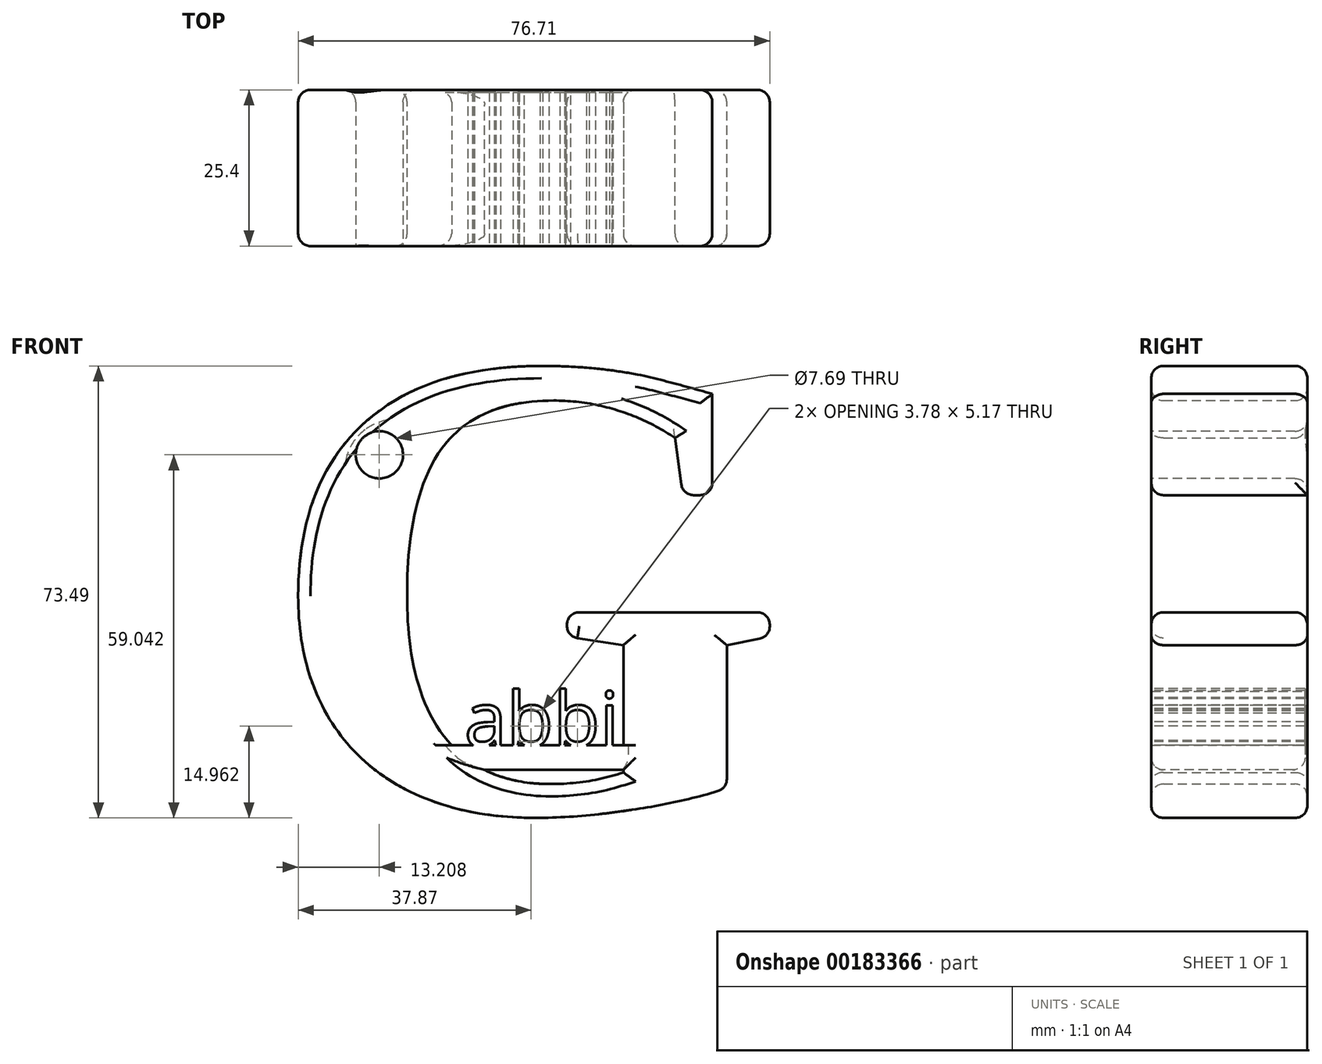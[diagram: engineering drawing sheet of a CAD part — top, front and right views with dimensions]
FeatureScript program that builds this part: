
annotation { "Feature Type Name" : "Feature", "Feature Type Description" : "" }
export const myFeature = defineFeature(function(context is Context, id is Id, definition is map)
    precondition{}
    {
        {
            var Q0;
            Q0=qCreatedBy(makeId("Front.planeOp"),FACE);
            var sketch = newSketch(context, id + "F0", { "sketchPlane" : qUnion([Q0])});
            skText(sketch, "E0", { "text": "G", "fontName": "Tinos-Bold.ttf"});
            const initialGuessF0  = {"E0": [-0.03052, -0.04578, 1, 0, 0.07873]};
            skSetInitialGuess(sketch, initialGuessF0);
            skSolve(sketch);
        }
        {
            var Q0;
            Q0 = qSketchRegion(id + "F0", true);
            extrude(context, id + "F1", {"entities" : qUnion([Q0]), "depth" : 25.4 * mm});
        }
        {
            var Q0;
            Q0=makeQuery(id+"F1.opExtrude","CAP_FACE",FACE,{"disambiguationData":[OSD([sQuery(id+"F0.wireOp",EDGE,"E0.sketch_text.stroke-0"),sQuery(id+"F0.wireOp",EDGE,"E0.sketch_text.stroke-1"),sQuery(id+"F0.wireOp",EDGE,"E0.sketch_text.stroke-2"),sQuery(id+"F0.wireOp",EDGE,"E0.sketch_text.stroke-3"),sQuery(id+"F0.wireOp",EDGE,"E0.sketch_text.stroke-4"),sQuery(id+"F0.wireOp",EDGE,"E0.sketch_text.stroke-5"),sQuery(id+"F0.wireOp",EDGE,"E0.sketch_text.stroke-6"),sQuery(id+"F0.wireOp",EDGE,"E0.sketch_text.stroke-7"),sQuery(id+"F0.wireOp",EDGE,"E0.sketch_text.stroke-8"),sQuery(id+"F0.wireOp",EDGE,"E0.sketch_text.stroke-9"),sQuery(id+"F0.wireOp",EDGE,"E0.sketch_text.stroke-10"),sQuery(id+"F0.wireOp",EDGE,"E0.sketch_text.stroke-11"),sQuery(id+"F0.wireOp",EDGE,"E0.sketch_text.stroke-12"),sQuery(id+"F0.wireOp",EDGE,"E0.sketch_text.stroke-13"),sQuery(id+"F0.wireOp",EDGE,"E0.sketch_text.stroke-14"),sQuery(id+"F0.wireOp",EDGE,"E0.sketch_text.stroke-15"),sQuery(id+"F0.wireOp",EDGE,"E0.sketch_text.stroke-16"),sQuery(id+"F0.wireOp",EDGE,"E0.sketch_text.stroke-17"),sQuery(id+"F0.wireOp",EDGE,"E0.sketch_text.stroke-18"),sQuery(id+"F0.wireOp",EDGE,"E0.sketch_text.stroke-19"),sQuery(id+"F0.wireOp",EDGE,"E0.sketch_text.stroke-20"),sQuery(id+"F0.wireOp",EDGE,"E0.sketch_text.stroke-21"),sQuery(id+"F0.wireOp",EDGE,"E0.sketch_text.stroke-22"),sQuery(id+"F0.wireOp",EDGE,"E0.sketch_text.stroke-23"),sQuery(id+"F0.wireOp",EDGE,"E0.sketch_text.stroke-24"),sQuery(id+"F0.wireOp",EDGE,"E0.sketch_text.stroke-25"),sQuery(id+"F0.wireOp",EDGE,"E0.sketch_text.stroke-26")])],"isStart":false});
            var sketch = newSketch(context, id + "F2", { "sketchPlane" : qUnion([Q0])});
            skCircle(sketch, "E1", {"center": v(-11.96, 12.18) * mm, "radius": 3.84 * mm});
            skSolve(sketch);
        }
        {
            var Q0;
            Q0=makeQuery(id+"F2.imprint","IMPRINT",FACE,{"disambiguationData":[TD([[makeQuery(id+"F2.imprint","IMPRINT",EDGE,{"derivedFrom":sQuery(id+"F2.wireOp",EDGE,"E1")}),1.0]])]});
            extrude(context, id + "F3", {"entities" : qUnion([Q0]), "operationType" : NewBodyOperationType.REMOVE, "oppositeDirection" : true, "depth" : 27.94 * mm});
        }
        {
            var Q0;
            Q0=makeQuery(id+"F1.opExtrude","CAP_EDGE",EDGE,{"disambiguationData":[OSD([sQuery(id+"F0.wireOp",EDGE,"E0.sketch_text.stroke-9")])],"isStart":false});
            var Q1;
            Q1=makeQuery(id+"F1.opExtrude","CAP_EDGE",EDGE,{"disambiguationData":[OSD([sQuery(id+"F0.wireOp",EDGE,"E0.sketch_text.stroke-15")])],"isStart":false});
            var Q2;
            Q2=makeQuery(id+"F1.opExtrude","CAP_EDGE",EDGE,{"disambiguationData":[OSD([sQuery(id+"F0.wireOp",EDGE,"E0.sketch_text.stroke-20")])],"isStart":false});
            var Q3;
            Q3=makeQuery(id+"F1.opExtrude","CAP_EDGE",EDGE,{"disambiguationData":[OSD([sQuery(id+"F0.wireOp",EDGE,"E0.sketch_text.stroke-21")])],"isStart":false});
            var Q4;
            Q4=makeQuery(id+"F1.opExtrude","CAP_EDGE",EDGE,{"disambiguationData":[OSD([sQuery(id+"F0.wireOp",EDGE,"E0.sketch_text.stroke-22")])],"isStart":false});
            var Q5;
            Q5=makeQuery(id+"F1.opExtrude","CAP_EDGE",EDGE,{"disambiguationData":[OSD([sQuery(id+"F0.wireOp",EDGE,"E0.sketch_text.stroke-24")])],"isStart":false});
            var Q6;
            Q6=makeQuery(id+"F1.opExtrude","CAP_EDGE",EDGE,{"disambiguationData":[OSD([sQuery(id+"F0.wireOp",EDGE,"E0.sketch_text.stroke-26")])],"isStart":false});
            var Q7;
            Q7=makeQuery(id+"F1.opExtrude","CAP_EDGE",EDGE,{"disambiguationData":[OSD([sQuery(id+"F0.wireOp",EDGE,"E0.sketch_text.stroke-23")])],"isStart":false});
            var Q8;
            Q8=makeQuery(id+"F1.opExtrude","CAP_EDGE",EDGE,{"disambiguationData":[OSD([sQuery(id+"F0.wireOp",EDGE,"E0.sketch_text.stroke-12")])],"isStart":false});
            var Q9;
            Q9=makeQuery(id+"F1.opExtrude","CAP_EDGE",EDGE,{"disambiguationData":[OSD([sQuery(id+"F0.wireOp",EDGE,"E0.sketch_text.stroke-10")])],"isStart":false});
            var Q10;
            Q10=makeQuery(id+"F1.opExtrude","CAP_EDGE",EDGE,{"disambiguationData":[OSD([sQuery(id+"F0.wireOp",EDGE,"E0.sketch_text.stroke-11")])],"isStart":false});
            var Q11;
            Q11=makeQuery(id+"F1.opExtrude","SWEPT_EDGE",EDGE,{"disambiguationData":[OSD([sQuery(id+"F0.wireOp",EDGE,"E0.sketch_text.stroke-11"),sQuery(id+"F0.wireOp",EDGE,"E0.sketch_text.stroke-12")])]});
            var Q12;
            Q12=makeQuery(id+"F1.opExtrude","SWEPT_EDGE",EDGE,{"disambiguationData":[OSD([sQuery(id+"F0.wireOp",EDGE,"E0.sketch_text.stroke-10"),sQuery(id+"F0.wireOp",EDGE,"E0.sketch_text.stroke-11")])]});
            var Q13;
            Q13=makeQuery(id+"F1.opExtrude","CAP_EDGE",EDGE,{"disambiguationData":[OSD([sQuery(id+"F0.wireOp",EDGE,"E0.sketch_text.stroke-25")])],"isStart":false});
            var Q14;
            Q14=makeQuery(id+"F3.boolean.opBoolean","COPY",EDGE,{"derivedFrom":makeQuery(id+"F3.opExtrude","CAP_EDGE",EDGE,{"disambiguationData":[OSD([sQuery(id+"F2.wireOp",EDGE,"E1")])],"isStart":true})});
            var Q15;
            Q15=makeQuery(id+"F3.boolean.opBoolean","INTERSECT",EDGE,{"derivedFrom":[makeQuery(id+"F1.opExtrude","CAP_FACE",FACE,{"disambiguationData":[OSD([sQuery(id+"F0.wireOp",EDGE,"E0.sketch_text.stroke-0"),sQuery(id+"F0.wireOp",EDGE,"E0.sketch_text.stroke-1"),sQuery(id+"F0.wireOp",EDGE,"E0.sketch_text.stroke-2"),sQuery(id+"F0.wireOp",EDGE,"E0.sketch_text.stroke-3"),sQuery(id+"F0.wireOp",EDGE,"E0.sketch_text.stroke-4"),sQuery(id+"F0.wireOp",EDGE,"E0.sketch_text.stroke-5"),sQuery(id+"F0.wireOp",EDGE,"E0.sketch_text.stroke-6"),sQuery(id+"F0.wireOp",EDGE,"E0.sketch_text.stroke-7"),sQuery(id+"F0.wireOp",EDGE,"E0.sketch_text.stroke-8"),sQuery(id+"F0.wireOp",EDGE,"E0.sketch_text.stroke-9"),sQuery(id+"F0.wireOp",EDGE,"E0.sketch_text.stroke-10"),sQuery(id+"F0.wireOp",EDGE,"E0.sketch_text.stroke-11"),sQuery(id+"F0.wireOp",EDGE,"E0.sketch_text.stroke-12"),sQuery(id+"F0.wireOp",EDGE,"E0.sketch_text.stroke-13"),sQuery(id+"F0.wireOp",EDGE,"E0.sketch_text.stroke-14"),sQuery(id+"F0.wireOp",EDGE,"E0.sketch_text.stroke-15"),sQuery(id+"F0.wireOp",EDGE,"E0.sketch_text.stroke-16"),sQuery(id+"F0.wireOp",EDGE,"E0.sketch_text.stroke-17"),sQuery(id+"F0.wireOp",EDGE,"E0.sketch_text.stroke-18"),sQuery(id+"F0.wireOp",EDGE,"E0.sketch_text.stroke-19"),sQuery(id+"F0.wireOp",EDGE,"E0.sketch_text.stroke-20"),sQuery(id+"F0.wireOp",EDGE,"E0.sketch_text.stroke-21"),sQuery(id+"F0.wireOp",EDGE,"E0.sketch_text.stroke-22"),sQuery(id+"F0.wireOp",EDGE,"E0.sketch_text.stroke-23"),sQuery(id+"F0.wireOp",EDGE,"E0.sketch_text.stroke-24"),sQuery(id+"F0.wireOp",EDGE,"E0.sketch_text.stroke-25"),sQuery(id+"F0.wireOp",EDGE,"E0.sketch_text.stroke-26")])],"isStart":true}),makeQuery(id+"F3.opExtrude","SWEPT_FACE",FACE,{"disambiguationData":[OSD([sQuery(id+"F2.wireOp",EDGE,"E1")])]})]});
            var Q16;
            Q16=makeQuery(id+"F1.opExtrude","CAP_EDGE",EDGE,{"disambiguationData":[OSD([sQuery(id+"F0.wireOp",EDGE,"E0.sketch_text.stroke-26")])],"isStart":true});
            var Q17;
            Q17=makeQuery(id+"F1.opExtrude","SWEPT_EDGE",EDGE,{"disambiguationData":[OSD([sQuery(id+"F0.wireOp",EDGE,"E0.sketch_text.stroke-0"),sQuery(id+"F0.wireOp",EDGE,"E0.sketch_text.stroke-26")])]});
            var Q18;
            Q18=makeQuery(id+"F1.opExtrude","CAP_EDGE",EDGE,{"disambiguationData":[OSD([sQuery(id+"F0.wireOp",EDGE,"E0.sketch_text.stroke-23")])],"isStart":true});
            var Q19;
            Q19=makeQuery(id+"F1.opExtrude","CAP_EDGE",EDGE,{"disambiguationData":[OSD([sQuery(id+"F0.wireOp",EDGE,"E0.sketch_text.stroke-22")])],"isStart":true});
            var Q20;
            Q20=makeQuery(id+"F1.opExtrude","SWEPT_EDGE",EDGE,{"disambiguationData":[OSD([sQuery(id+"F0.wireOp",EDGE,"E0.sketch_text.stroke-22"),sQuery(id+"F0.wireOp",EDGE,"E0.sketch_text.stroke-23")])]});
            var Q21;
            Q21=makeQuery(id+"F1.opExtrude","SWEPT_EDGE",EDGE,{"disambiguationData":[OSD([sQuery(id+"F0.wireOp",EDGE,"E0.sketch_text.stroke-24"),sQuery(id+"F0.wireOp",EDGE,"E0.sketch_text.stroke-25")])]});
            var Q22;
            Q22=makeQuery(id+"F1.opExtrude","SWEPT_EDGE",EDGE,{"disambiguationData":[OSD([sQuery(id+"F0.wireOp",EDGE,"E0.sketch_text.stroke-23"),sQuery(id+"F0.wireOp",EDGE,"E0.sketch_text.stroke-24")])]});
            var Q23;
            Q23=makeQuery(id+"F1.opExtrude","CAP_EDGE",EDGE,{"disambiguationData":[OSD([sQuery(id+"F0.wireOp",EDGE,"E0.sketch_text.stroke-9")])],"isStart":true});
            var Q24;
            Q24=makeQuery(id+"F1.opExtrude","CAP_EDGE",EDGE,{"disambiguationData":[OSD([sQuery(id+"F0.wireOp",EDGE,"E0.sketch_text.stroke-10")])],"isStart":true});
            fillet(context, id + "F4", {"entities" : qUnion([Q0, Q1, Q2, Q3, Q4, Q5, Q6, Q7, Q8, Q9, Q10, Q11, Q12, Q13, Q14, Q15, Q16, Q17, Q18, Q19, Q20, Q21, Q22, Q23, Q24]), "radius" : 2 * mm, "tangentPropagation" : true, "allowEdgeOverflow" : false});
        }
        {
            var Q0;
            Q0=makeQuery(id+"F1.opExtrude","CAP_EDGE",EDGE,{"disambiguationData":[OSD([sQuery(id+"F0.wireOp",EDGE,"E0.sketch_text.stroke-15")])],"isStart":true});
            var Q1;
            Q1=makeQuery(id+"F1.opExtrude","CAP_EDGE",EDGE,{"disambiguationData":[OSD([sQuery(id+"F0.wireOp",EDGE,"E0.sketch_text.stroke-21")])],"isStart":true});
            var Q2;
            Q2=makeQuery(id+"F1.opExtrude","CAP_EDGE",EDGE,{"disambiguationData":[OSD([sQuery(id+"F0.wireOp",EDGE,"E0.sketch_text.stroke-20")])],"isStart":true});
            fillet(context, id + "F5", {"entities" : qUnion([Q0, Q1, Q2]), "radius" : 2 * mm, "tangentPropagation" : true, "allowEdgeOverflow" : false});
        }
        {
            var Q0;
            Q0=makeQuery(id+"F1.opExtrude","CAP_FACE",FACE,{"disambiguationData":[OSD([sQuery(id+"F0.wireOp",EDGE,"E0.sketch_text.stroke-0"),sQuery(id+"F0.wireOp",EDGE,"E0.sketch_text.stroke-1"),sQuery(id+"F0.wireOp",EDGE,"E0.sketch_text.stroke-2"),sQuery(id+"F0.wireOp",EDGE,"E0.sketch_text.stroke-3"),sQuery(id+"F0.wireOp",EDGE,"E0.sketch_text.stroke-4"),sQuery(id+"F0.wireOp",EDGE,"E0.sketch_text.stroke-5"),sQuery(id+"F0.wireOp",EDGE,"E0.sketch_text.stroke-6"),sQuery(id+"F0.wireOp",EDGE,"E0.sketch_text.stroke-7"),sQuery(id+"F0.wireOp",EDGE,"E0.sketch_text.stroke-8"),sQuery(id+"F0.wireOp",EDGE,"E0.sketch_text.stroke-9"),sQuery(id+"F0.wireOp",EDGE,"E0.sketch_text.stroke-10"),sQuery(id+"F0.wireOp",EDGE,"E0.sketch_text.stroke-11"),sQuery(id+"F0.wireOp",EDGE,"E0.sketch_text.stroke-12"),sQuery(id+"F0.wireOp",EDGE,"E0.sketch_text.stroke-13"),sQuery(id+"F0.wireOp",EDGE,"E0.sketch_text.stroke-14"),sQuery(id+"F0.wireOp",EDGE,"E0.sketch_text.stroke-15"),sQuery(id+"F0.wireOp",EDGE,"E0.sketch_text.stroke-16"),sQuery(id+"F0.wireOp",EDGE,"E0.sketch_text.stroke-17"),sQuery(id+"F0.wireOp",EDGE,"E0.sketch_text.stroke-18"),sQuery(id+"F0.wireOp",EDGE,"E0.sketch_text.stroke-19"),sQuery(id+"F0.wireOp",EDGE,"E0.sketch_text.stroke-20"),sQuery(id+"F0.wireOp",EDGE,"E0.sketch_text.stroke-21"),sQuery(id+"F0.wireOp",EDGE,"E0.sketch_text.stroke-22"),sQuery(id+"F0.wireOp",EDGE,"E0.sketch_text.stroke-23"),sQuery(id+"F0.wireOp",EDGE,"E0.sketch_text.stroke-24"),sQuery(id+"F0.wireOp",EDGE,"E0.sketch_text.stroke-25"),sQuery(id+"F0.wireOp",EDGE,"E0.sketch_text.stroke-26")])],"isStart":false});
            var sketch = newSketch(context, id + "F6", { "sketchPlane" : qUnion([Q0])});
            skText(sketch, "E2", { "text": "abbi\n", "fontName": "OpenSans-Regular.ttf"});
            skLineSegment(sketch, "E3.bottom", {"start": v(-3.16, -35.04) * mm, "end": v(30.97, -35.04) * mm});
            skLineSegment(sketch, "E3.top", {"start": v(-3.16, -39.06) * mm, "end": v(30.97, -39.06) * mm});
            skLineSegment(sketch, "E3.left", {"start": v(-3.16, -35.04) * mm, "end": v(-3.16, -39.06) * mm});
            skLineSegment(sketch, "E3.right", {"start": v(30.97, -35.04) * mm, "end": v(30.97, -39.06) * mm});
            const initialGuessF6  = {"E2": [0.00187, -0.0352, 1, 0, 0.0089]};
            skSetInitialGuess(sketch, initialGuessF6);
            skSolve(sketch);
        }
        {
            var Q0;
            Q0 = qSketchRegion(id + "F6", true);
            extrude(context, id + "F7", {"entities" : qUnion([Q0]), "operationType" : NewBodyOperationType.ADD, "oppositeDirection" : true, "depth" : 25 * mm});
        }
        {
            var Q0;
            Q0=makeQuery(id+"F7.opExtrude","CAP_EDGE",EDGE,{"disambiguationData":[OSD([sQuery(id+"F6.wireOp",EDGE,"E3.top")])],"isStart":true});
            var Q1;
            Q1=makeQuery(id+"F7.opExtrude","CAP_EDGE",EDGE,{"disambiguationData":[OSD([sQuery(id+"F6.wireOp",EDGE,"E3.top")])],"isStart":false});
            var Q2;
            {var subQ0=sQuery(id+"F0.wireOp",EDGE,"E0.sketch_text.stroke-25");var subQ1=sQuery(id+"F0.wireOp",EDGE,"E0.sketch_text.stroke-24");Q2=makeQuery(id+"F4.opFillet","BLEND_EDGE",EDGE,{"blendedFrom":[makeQuery(id+"F1.opExtrude","SWEPT_EDGE",EDGE,{"disambiguationData":[OSD([subQ1,subQ0])]}),makeQuery(id+"F1.opExtrude","CAP_FACE",FACE,{"disambiguationData":[OSD([sQuery(id+"F0.wireOp",EDGE,"E0.sketch_text.stroke-0"),sQuery(id+"F0.wireOp",EDGE,"E0.sketch_text.stroke-1"),sQuery(id+"F0.wireOp",EDGE,"E0.sketch_text.stroke-2"),sQuery(id+"F0.wireOp",EDGE,"E0.sketch_text.stroke-3"),sQuery(id+"F0.wireOp",EDGE,"E0.sketch_text.stroke-4"),sQuery(id+"F0.wireOp",EDGE,"E0.sketch_text.stroke-5"),sQuery(id+"F0.wireOp",EDGE,"E0.sketch_text.stroke-6"),sQuery(id+"F0.wireOp",EDGE,"E0.sketch_text.stroke-7"),sQuery(id+"F0.wireOp",EDGE,"E0.sketch_text.stroke-8"),sQuery(id+"F0.wireOp",EDGE,"E0.sketch_text.stroke-9"),sQuery(id+"F0.wireOp",EDGE,"E0.sketch_text.stroke-10"),sQuery(id+"F0.wireOp",EDGE,"E0.sketch_text.stroke-11"),sQuery(id+"F0.wireOp",EDGE,"E0.sketch_text.stroke-12"),sQuery(id+"F0.wireOp",EDGE,"E0.sketch_text.stroke-13"),sQuery(id+"F0.wireOp",EDGE,"E0.sketch_text.stroke-14"),sQuery(id+"F0.wireOp",EDGE,"E0.sketch_text.stroke-15"),sQuery(id+"F0.wireOp",EDGE,"E0.sketch_text.stroke-16"),sQuery(id+"F0.wireOp",EDGE,"E0.sketch_text.stroke-17"),sQuery(id+"F0.wireOp",EDGE,"E0.sketch_text.stroke-18"),sQuery(id+"F0.wireOp",EDGE,"E0.sketch_text.stroke-19"),sQuery(id+"F0.wireOp",EDGE,"E0.sketch_text.stroke-20"),sQuery(id+"F0.wireOp",EDGE,"E0.sketch_text.stroke-21"),sQuery(id+"F0.wireOp",EDGE,"E0.sketch_text.stroke-22"),sQuery(id+"F0.wireOp",EDGE,"E0.sketch_text.stroke-23"),subQ1,subQ0,sQuery(id+"F0.wireOp",EDGE,"E0.sketch_text.stroke-26")])],"isStart":true})],"blendedInto":[makeQuery(id+"F1.opExtrude","CAP_FACE",FACE,{"disambiguationData":[OSD([sQuery(id+"F0.wireOp",EDGE,"E0.sketch_text.stroke-0"),sQuery(id+"F0.wireOp",EDGE,"E0.sketch_text.stroke-1"),sQuery(id+"F0.wireOp",EDGE,"E0.sketch_text.stroke-2"),sQuery(id+"F0.wireOp",EDGE,"E0.sketch_text.stroke-3"),sQuery(id+"F0.wireOp",EDGE,"E0.sketch_text.stroke-4"),sQuery(id+"F0.wireOp",EDGE,"E0.sketch_text.stroke-5"),sQuery(id+"F0.wireOp",EDGE,"E0.sketch_text.stroke-6"),sQuery(id+"F0.wireOp",EDGE,"E0.sketch_text.stroke-7"),sQuery(id+"F0.wireOp",EDGE,"E0.sketch_text.stroke-8"),sQuery(id+"F0.wireOp",EDGE,"E0.sketch_text.stroke-9"),sQuery(id+"F0.wireOp",EDGE,"E0.sketch_text.stroke-10"),sQuery(id+"F0.wireOp",EDGE,"E0.sketch_text.stroke-11"),sQuery(id+"F0.wireOp",EDGE,"E0.sketch_text.stroke-12"),sQuery(id+"F0.wireOp",EDGE,"E0.sketch_text.stroke-13"),sQuery(id+"F0.wireOp",EDGE,"E0.sketch_text.stroke-14"),sQuery(id+"F0.wireOp",EDGE,"E0.sketch_text.stroke-15"),sQuery(id+"F0.wireOp",EDGE,"E0.sketch_text.stroke-16"),sQuery(id+"F0.wireOp",EDGE,"E0.sketch_text.stroke-17"),sQuery(id+"F0.wireOp",EDGE,"E0.sketch_text.stroke-18"),sQuery(id+"F0.wireOp",EDGE,"E0.sketch_text.stroke-19"),sQuery(id+"F0.wireOp",EDGE,"E0.sketch_text.stroke-20"),sQuery(id+"F0.wireOp",EDGE,"E0.sketch_text.stroke-21"),sQuery(id+"F0.wireOp",EDGE,"E0.sketch_text.stroke-22"),sQuery(id+"F0.wireOp",EDGE,"E0.sketch_text.stroke-23"),subQ1,subQ0,sQuery(id+"F0.wireOp",EDGE,"E0.sketch_text.stroke-26")])],"isStart":true})]});}
            fillet(context, id + "F8", {"entities" : qUnion([Q0, Q1, Q2]), "radius" : 2 * mm, "tangentPropagation" : true, "allowEdgeOverflow" : false});
        }
    });
